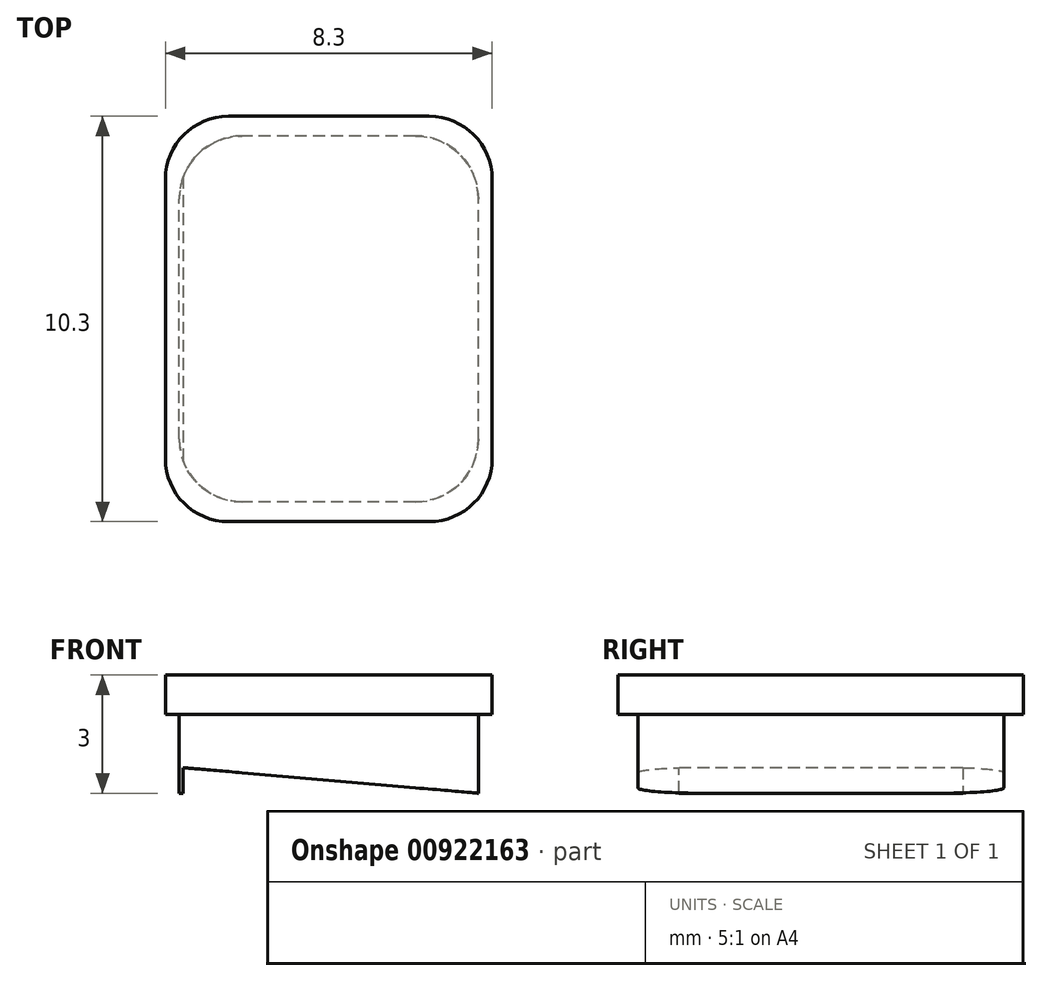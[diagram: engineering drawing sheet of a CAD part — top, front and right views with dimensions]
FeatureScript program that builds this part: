
annotation { "Feature Type Name" : "Feature", "Feature Type Description" : "" }
export const myFeature = defineFeature(function(context is Context, id is Id, definition is map)
    precondition{}
    {
        {
            var Q0;
            Q0=qCreatedBy(makeId("Top.planeOp"),FACE);
            var sketch = newSketch(context, id + "F0", { "sketchPlane" : qUnion([Q0])});
            skLineSegment(sketch, "E0.bottom", {"start": v(3.8, -4.65) * mm, "end": v(-3.8, -4.65) * mm});
            skLineSegment(sketch, "E0.top", {"start": v(3.8, 4.65) * mm, "end": v(-3.8, 4.65) * mm});
            skLineSegment(sketch, "E0.left", {"start": v(3.8, -4.65) * mm, "end": v(3.8, 4.65) * mm});
            skLineSegment(sketch, "E0.right", {"start": v(-3.8, -4.65) * mm, "end": v(-3.8, 4.65) * mm});
            skPoint(sketch, "E0.middle", {"position": v(0, 0) * mm});
            skLineSegment(sketch, "E1.bottom", {"start": v(4.15, -5.15) * mm, "end": v(-4.15, -5.15) * mm});
            skLineSegment(sketch, "E1.top", {"start": v(4.15, 5.15) * mm, "end": v(-4.15, 5.15) * mm});
            skLineSegment(sketch, "E1.left", {"start": v(4.15, -5.15) * mm, "end": v(4.15, 5.15) * mm});
            skLineSegment(sketch, "E1.right", {"start": v(-4.15, -5.15) * mm, "end": v(-4.15, 5.15) * mm});
            skSolve(sketch);
        }
        {
            var Q0;
            Q0=makeQuery(id+"F0.imprint","IMPRINT",FACE,{"disambiguationData":[TD([[makeQuery(id+"F0.imprint","IMPRINT",EDGE,{"derivedFrom":sQuery(id+"F0.wireOp",EDGE,"E0.bottom")}),1.0]])]});
            var Q1;
            Q1=makeQuery(id+"F0.imprint","IMPRINT",FACE,{"disambiguationData":[TD([[makeQuery(id+"F0.imprint","IMPRINT",EDGE,{"derivedFrom":sQuery(id+"F0.wireOp",EDGE,"E0.bottom")}),-1.0]])]});
            extrude(context, id + "F1", {"entities" : qUnion([Q0, Q1]), "depth" : 1 * mm, "offsetDistance" : 25 * mm});
        }
        {
            var Q0;
            Q0=makeQuery(id+"F0.imprint","IMPRINT",FACE,{"disambiguationData":[TD([[makeQuery(id+"F0.imprint","IMPRINT",EDGE,{"derivedFrom":sQuery(id+"F0.wireOp",EDGE,"E0.bottom")}),-1.0]])]});
            extrude(context, id + "F2", {"entities" : qUnion([Q0]), "operationType" : NewBodyOperationType.ADD, "oppositeDirection" : true, "depth" : 2 * mm, "offsetDistance" : 25 * mm});
        }
        {
            var Q0;
            Q0=makeQuery(id+"F1.opExtrude","SWEPT_EDGE",EDGE,{"disambiguationData":[OSD([sQuery(id+"F0.wireOp",EDGE,"E1.top"),sQuery(id+"F0.wireOp",EDGE,"E1.right")])]});
            var Q1;
            Q1=makeQuery(id+"F1.opExtrude","SWEPT_EDGE",EDGE,{"disambiguationData":[OSD([sQuery(id+"F0.wireOp",EDGE,"E1.bottom"),sQuery(id+"F0.wireOp",EDGE,"E1.right")])]});
            var Q2;
            Q2=makeQuery(id+"F1.opExtrude","SWEPT_EDGE",EDGE,{"disambiguationData":[OSD([sQuery(id+"F0.wireOp",EDGE,"E1.top"),sQuery(id+"F0.wireOp",EDGE,"E1.left")])]});
            var Q3;
            Q3=makeQuery(id+"F1.opExtrude","SWEPT_EDGE",EDGE,{"disambiguationData":[OSD([sQuery(id+"F0.wireOp",EDGE,"E1.bottom"),sQuery(id+"F0.wireOp",EDGE,"E1.left")])]});
            var Q4;
            Q4=makeQuery(id+"F2.opExtrude","SWEPT_EDGE",EDGE,{"disambiguationData":[OSD([sQuery(id+"F0.wireOp",EDGE,"E0.bottom"),sQuery(id+"F0.wireOp",EDGE,"E0.left")])]});
            var Q5;
            Q5=makeQuery(id+"F2.opExtrude","SWEPT_EDGE",EDGE,{"disambiguationData":[OSD([sQuery(id+"F0.wireOp",EDGE,"E0.top"),sQuery(id+"F0.wireOp",EDGE,"E0.left")])]});
            var Q6;
            Q6=makeQuery(id+"F2.opExtrude","SWEPT_EDGE",EDGE,{"disambiguationData":[OSD([sQuery(id+"F0.wireOp",EDGE,"E0.bottom"),sQuery(id+"F0.wireOp",EDGE,"E0.right")])]});
            var Q7;
            Q7=makeQuery(id+"F2.opExtrude","SWEPT_EDGE",EDGE,{"disambiguationData":[OSD([sQuery(id+"F0.wireOp",EDGE,"E0.top"),sQuery(id+"F0.wireOp",EDGE,"E0.right")])]});
            fillet(context, id + "F3", {"entities" : qUnion([Q0, Q1, Q2, Q3, Q4, Q5, Q6, Q7]), "radius" : 1.6 * mm, "tangentPropagation" : true, "allowEdgeOverflow" : false});
        }
        {
            var Q0;
            Q0=qCreatedBy(makeId("Front.planeOp"),FACE);
            var sketch = newSketch(context, id + "F4", { "sketchPlane" : qUnion([Q0])});
            skLineSegment(sketch, "E2", {"start": v(-3.7, -1.35) * mm, "end": v(3.8, -2) * mm});
            skLineSegment(sketch, "E3", {"start": v(-3.7, -1.35) * mm, "end": v(-3.7, -2.17) * mm});
            skLineSegment(sketch, "E4", {"start": v(-3.7, -2.17) * mm, "end": v(3.8, -2) * mm});
            skSolve(sketch);
        }
        {
            var Q0;
            Q0=qSketchRegion(id+"F4",true);
            extrude(context, id + "F5", {"entities" : qUnion([Q0]), "operationType" : NewBodyOperationType.REMOVE, "endBound" : BoundingType.SYMMETRIC, "oppositeDirection" : true, "depth" : 100 * mm, "offsetDistance" : 25 * mm});
        }
    });
